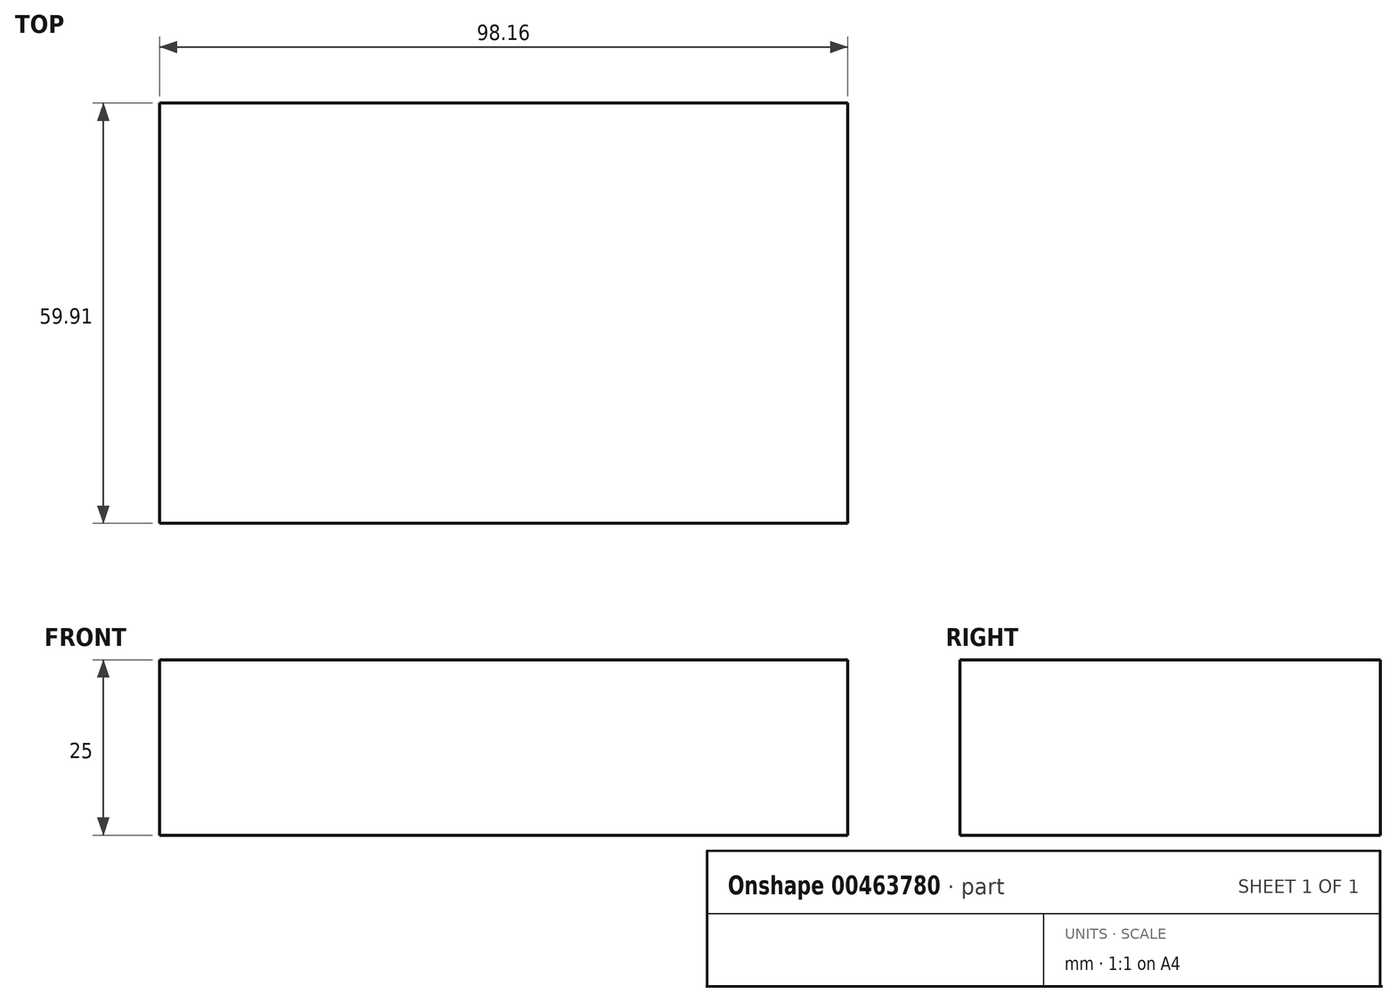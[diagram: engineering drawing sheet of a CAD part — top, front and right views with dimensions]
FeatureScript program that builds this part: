
annotation { "Feature Type Name" : "Feature", "Feature Type Description" : "" }
export const myFeature = defineFeature(function(context is Context, id is Id, definition is map)
    precondition{}
    {
        {
            var Q0;
            Q0=qCreatedBy(makeId("Top.planeOp"),FACE);
            var sketch = newSketch(context, id + "F0", { "sketchPlane" : qUnion([Q0])});
            skLineSegment(sketch, "E0.bottom", {"start": v(-47.59, 37.14) * mm, "end": v(50.57, 37.14) * mm});
            skLineSegment(sketch, "E0.top", {"start": v(-47.59, -22.77) * mm, "end": v(50.57, -22.77) * mm});
            skLineSegment(sketch, "E0.left", {"start": v(-47.59, 37.14) * mm, "end": v(-47.59, -22.77) * mm});
            skLineSegment(sketch, "E0.right", {"start": v(50.57, 37.14) * mm, "end": v(50.57, -22.77) * mm});
            skSolve(sketch);
        }
        {
            var Q0;
            Q0 = qSketchRegion(id + "F0", true);
            extrude(context, id + "F1", {"entities" : qUnion([Q0]), "depth" : 25 * mm});
        }
    });
